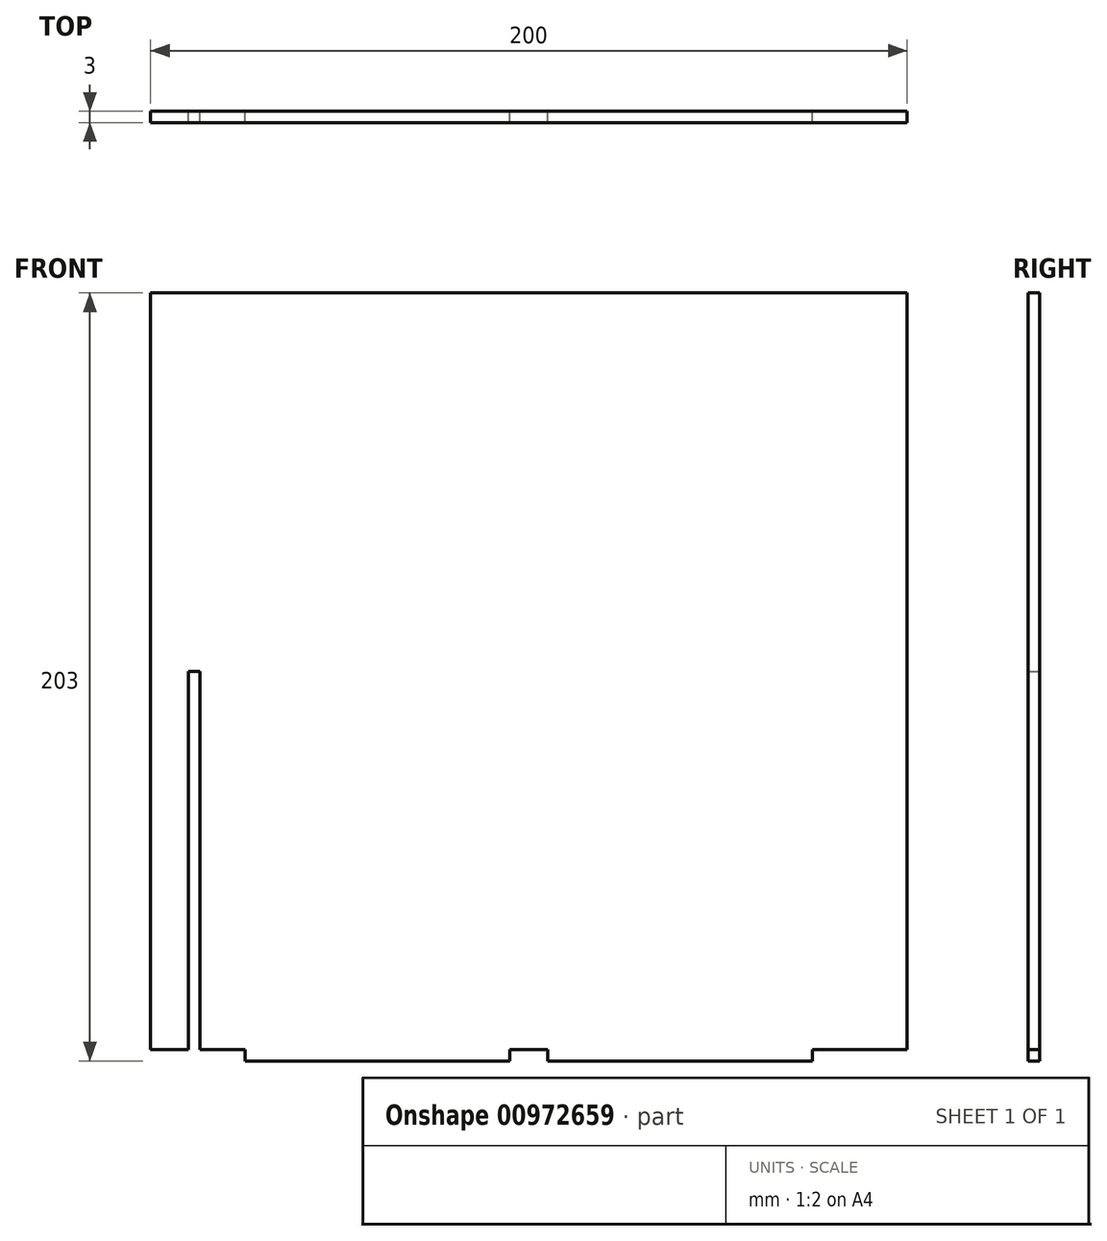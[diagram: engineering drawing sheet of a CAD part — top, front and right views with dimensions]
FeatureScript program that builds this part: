
annotation { "Feature Type Name" : "Feature", "Feature Type Description" : "" }
export const myFeature = defineFeature(function(context is Context, id is Id, definition is map)
    precondition{}
    {
        {
            var Q0;
            Q0=qCreatedBy(makeId("Front.planeOp"),FACE);
            var sketch = newSketch(context, id + "F0", { "sketchPlane" : qUnion([Q0])});
            skLineSegment(sketch, "E0.bottom", {"start": v(-81.86, 146.71) * mm, "end": v(118.14, 146.71) * mm});
            skLineSegment(sketch, "E0.top", {"start": v(-81.86, -53.29) * mm, "end": v(118.14, -53.29) * mm});
            skLineSegment(sketch, "E0.left", {"start": v(-81.86, 146.71) * mm, "end": v(-81.86, -53.29) * mm});
            skLineSegment(sketch, "E0.right", {"start": v(118.14, 146.71) * mm, "end": v(118.14, -53.29) * mm});
            skLineSegment(sketch, "E1.bottom", {"start": v(-71.86, -53.29) * mm, "end": v(-68.86, -53.29) * mm});
            skLineSegment(sketch, "E1.top", {"start": v(-71.86, 46.71) * mm, "end": v(-68.86, 46.71) * mm});
            skLineSegment(sketch, "E1.left", {"start": v(-71.86, -53.29) * mm, "end": v(-71.86, 46.71) * mm});
            skLineSegment(sketch, "E1.right", {"start": v(-68.86, -53.29) * mm, "end": v(-68.86, 46.71) * mm});
            skPoint(sketch, "E2", {"position": v(-81.86, 46.71) * mm});
            skPoint(sketch, "E3", {"position": v(18.14, -53.29) * mm});
            skLineSegment(sketch, "E4", {"start": v(93.14, -53.29) * mm, "end": v(93.14, -56.29) * mm});
            skLineSegment(sketch, "E5", {"start": v(93.14, -56.29) * mm, "end": v(23.14, -56.29) * mm});
            skLineSegment(sketch, "E6", {"start": v(23.14, -56.29) * mm, "end": v(23.14, -53.29) * mm});
            skLineSegment(sketch, "E7", {"start": v(13.14, -53.29) * mm, "end": v(13.14, -56.29) * mm});
            skLineSegment(sketch, "E8", {"start": v(13.14, -56.29) * mm, "end": v(-56.86, -56.29) * mm});
            skLineSegment(sketch, "E9", {"start": v(-56.86, -56.29) * mm, "end": v(-56.86, -53.29) * mm});
            skSolve(sketch);
        }
        {
            var Q0;
            Q0=makeQuery(id+"F0.imprint","IMPRINT",FACE,{"disambiguationData":[TD([[makeQuery(id+"F0.imprint","IMPRINT",EDGE,{"derivedFrom":sQuery(id+"F0.wireOp",EDGE,"E0.bottom")}),-1.0]])]});
            var Q1;
            {var subQ0=sQuery(id+"F0.wireOp",EDGE,"E4");Q1=makeQuery(id+"F0.imprint","IMPRINT",FACE,{"disambiguationData":[TD([[makeQuery(id+"F0.imprint","IMPRINT",EDGE,{"derivedFrom":subQ0}),-1.0]])]});}
            var Q2;
            {var subQ2=sQuery(id+"F0.wireOp",EDGE,"E7");Q2=makeQuery(id+"F0.imprint","IMPRINT",FACE,{"disambiguationData":[TD([[makeQuery(id+"F0.imprint","IMPRINT",EDGE,{"derivedFrom":subQ2}),-1.0]])]});}
            extrude(context, id + "F1", {"entities" : qUnion([Q0, Q1, Q2]), "depth" : 3 * mm, "offsetDistance" : 25 * mm});
        }
    });
